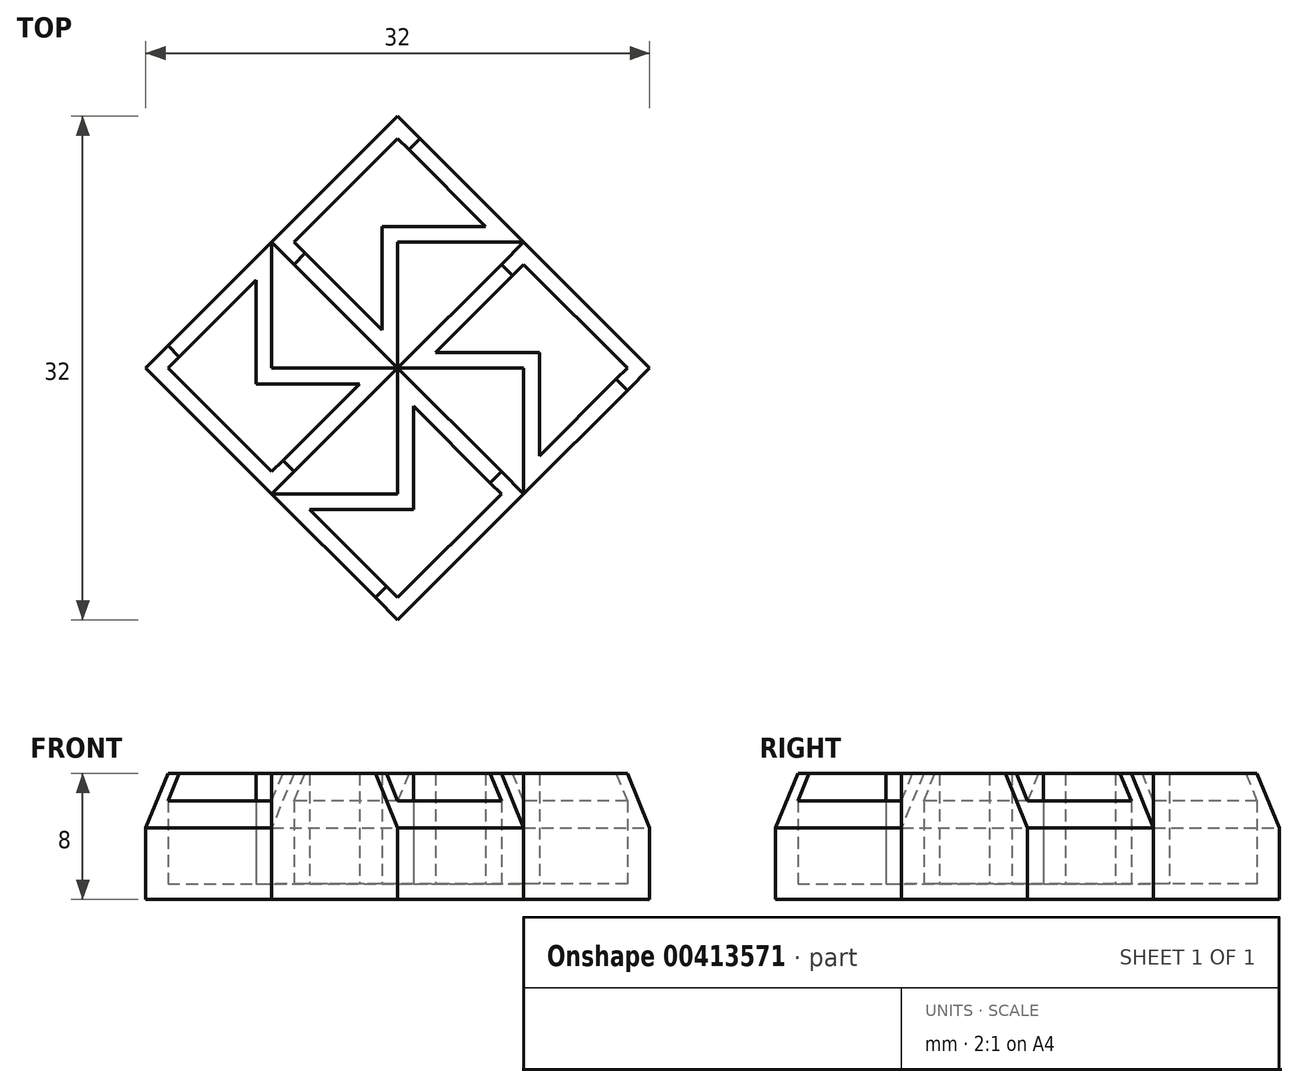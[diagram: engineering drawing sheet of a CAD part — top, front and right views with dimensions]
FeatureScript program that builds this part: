
annotation { "Feature Type Name" : "Feature", "Feature Type Description" : "" }
export const myFeature = defineFeature(function(context is Context, id is Id, definition is map)
    precondition{}
    {
        {
            var Q0;
            Q0=qCreatedBy(makeId("Top.planeOp"),FACE);
            var sketch = newSketch(context, id + "F0", { "sketchPlane" : qUnion([Q0])});
            skLineSegment(sketch, "E0", {"start": v(0, 0) * mm, "end": v(0, 8) * mm});
            skLineSegment(sketch, "E1", {"start": v(0, -8) * mm, "end": v(8, 0) * mm});
            skLineSegment(sketch, "E2", {"start": v(8, 0) * mm, "end": v(0, 0) * mm});
            skLineSegment(sketch, "E3.MirrorCS", {"start": v(0, 8) * mm, "end": v(8, 0) * mm});
            skLineSegment(sketch, "E4.MirrorCS", {"start": v(0, 0) * mm, "end": v(0, -8) * mm});
            skLineSegment(sketch, "E5", {"start": v(0, -11.82) * mm, "end": v(0, 11.77) * mm, "construction": true});
            skLineSegment(sketch, "E6.MirrorCS", {"start": v(0, 8) * mm, "end": v(-8, 0) * mm});
            skLineSegment(sketch, "E7.MirrorCS", {"start": v(0, -8) * mm, "end": v(-8, 0) * mm});
            skSolve(sketch);
        }
        {
            var Q0;
            Q0=makeQuery(id+"F0.imprint","IMPRINT",FACE,{"disambiguationData":[TD([[makeQuery(id+"F0.imprint","IMPRINT",EDGE,{"derivedFrom":sQuery(id+"F0.wireOp",EDGE,"E0")}),-1.0]])]});
            var Q1;
            Q1=makeQuery(id+"F0.imprint","IMPRINT",FACE,{"disambiguationData":[TD([[makeQuery(id+"F0.imprint","IMPRINT",EDGE,{"derivedFrom":sQuery(id+"F0.wireOp",EDGE,"E0")}),1.0]])]});
            extrude(context, id + "F1", {"entities" : qUnion([Q0, Q1]), "depth" : 8 * mm, "offsetDistance" : 25.4 * mm});
        }
        {
            var Q0;
            Q0=makeQuery(id+"F1.opExtrude","CAP_FACE",FACE,{"disambiguationData":[OSD([sQuery(id+"F0.wireOp",EDGE,"E2"),sQuery(id+"F0.wireOp",EDGE,"E3.MirrorCS"),sQuery(id+"F0.wireOp",EDGE,"E4.MirrorCS"),sQuery(id+"F0.wireOp",EDGE,"E6.MirrorCS"),sQuery(id+"F0.wireOp",EDGE,"E7.MirrorCS")])],"isStart":false});
            shell(context, id + "F2", {"entities" : qUnion([Q0]), "thickness" : 1 * mm});
        }
        {
            var Q0;
            Q0=makeQuery(id+"F1.opExtrude","CAP_EDGE",EDGE,{"disambiguationData":[OSD([sQuery(id+"F0.wireOp",EDGE,"E6.MirrorCS")])],"isStart":false});
            chamfer(context, id + "F3", {"entities" : qUnion([Q0]), "chamferType" : ChamferType.OFFSET_ANGLE, "width" : 2 * mm, "oppositeDirection" : false, "angle" : 60 * degree, "tangentPropagation" : true});
        }
        {
            var Q0;
            Q0=makeQuery(id+"F1.opExtrude","SWEPT_BODY",BODY,{"disambiguationData":[OSD([sQuery(id+"F0.wireOp",EDGE,"E2"),sQuery(id+"F0.wireOp",EDGE,"E3.MirrorCS"),sQuery(id+"F0.wireOp",EDGE,"E4.MirrorCS"),sQuery(id+"F0.wireOp",EDGE,"E6.MirrorCS"),sQuery(id+"F0.wireOp",EDGE,"E7.MirrorCS")])]});
            var Q1;
            Q1=makeQuery(id+"F1.opExtrude","SWEPT_EDGE",EDGE,{"disambiguationData":[OSD([sQuery(id+"F0.wireOp",EDGE,"E1"),sQuery(id+"F0.wireOp",EDGE,"E4.MirrorCS"),sQuery(id+"F0.wireOp",EDGE,"E7.MirrorCS")])]});
            circularPattern(context, id + "F4", {"entities" : qUnion([Q0]), "axis" : qUnion([Q1]), "angle" : 360 * degree, "instanceCount" : 4, "equalSpace" : true});
        }
    });
